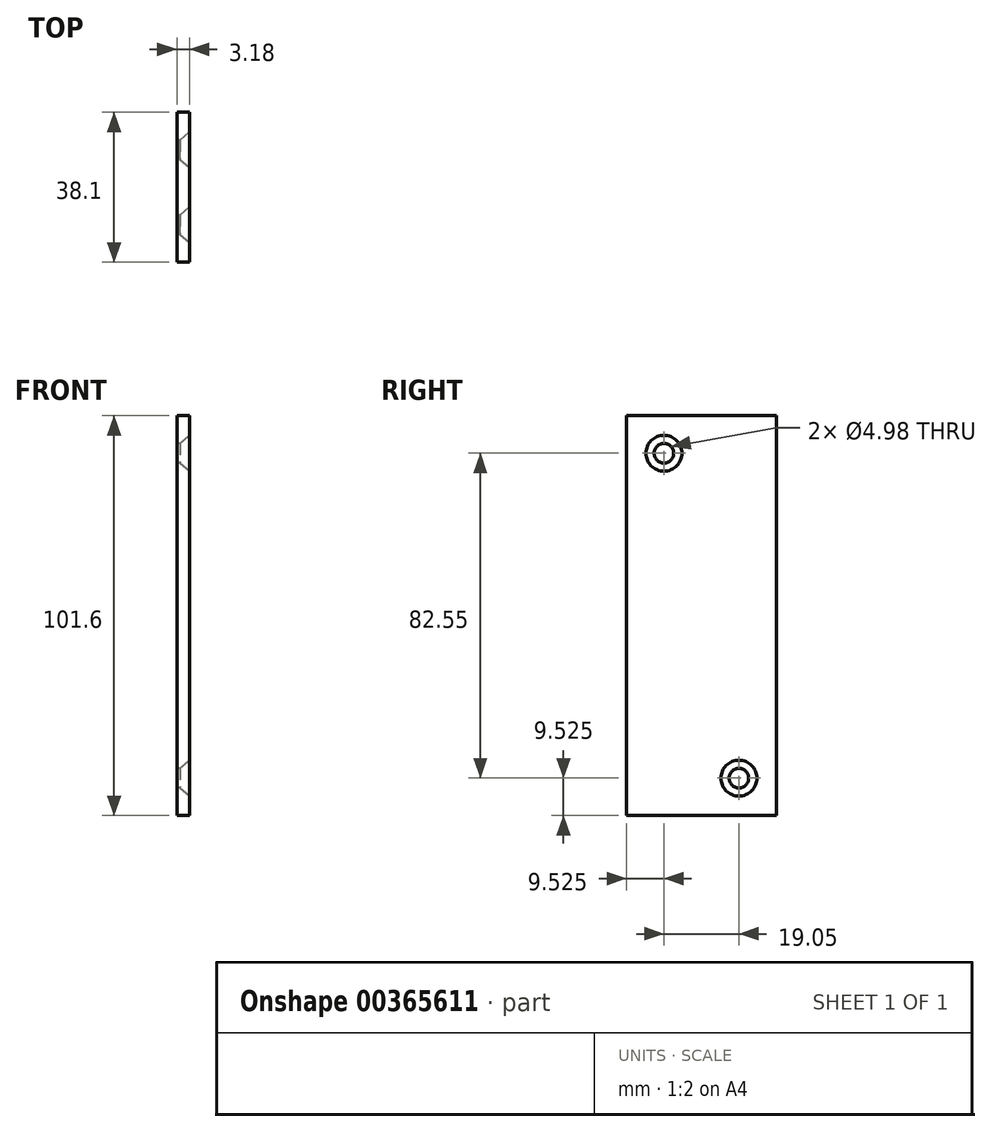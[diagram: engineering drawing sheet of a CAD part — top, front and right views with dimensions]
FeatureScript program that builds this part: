
annotation { "Feature Type Name" : "Feature", "Feature Type Description" : "" }
export const myFeature = defineFeature(function(context is Context, id is Id, definition is map)
    precondition{}
    {
        {
            var Q0;
            Q0=qCreatedBy(makeId("Right.planeOp"),FACE);
            var sketch = newSketch(context, id + "F0", { "sketchPlane" : qUnion([Q0])});
            skLineSegment(sketch, "E0.bottom", {"start": v(19.05, -50.8) * mm, "end": v(-19.05, -50.8) * mm});
            skLineSegment(sketch, "E0.top", {"start": v(19.05, 50.8) * mm, "end": v(-19.05, 50.8) * mm});
            skLineSegment(sketch, "E0.left", {"start": v(19.05, -50.8) * mm, "end": v(19.05, 50.8) * mm});
            skLineSegment(sketch, "E0.right", {"start": v(-19.05, -50.8) * mm, "end": v(-19.05, 50.8) * mm});
            skPoint(sketch, "E0.middle", {"position": v(0, 0) * mm});
            skSolve(sketch);
        }
        {
            var Q0;
            Q0=qSketchRegion(id+"F0",true);
            extrude(context, id + "F1", {"entities" : qUnion([Q0]), "depth" : 3.17 * mm, "offsetDistance" : 25.4 * mm});
        }
        {
            var Q0;
            Q0=makeQuery(id+"F1.opExtrude","CAP_FACE",FACE,{"disambiguationData":[OSD([sQuery(id+"F0.wireOp",EDGE,"E0.bottom"),sQuery(id+"F0.wireOp",EDGE,"E0.top"),sQuery(id+"F0.wireOp",EDGE,"E0.left"),sQuery(id+"F0.wireOp",EDGE,"E0.right")])],"isStart":false});
            var sketch = newSketch(context, id + "F2", { "sketchPlane" : qUnion([Q0])});
            skPoint(sketch, "E1", {"position": v(-9.53, 41.28) * mm});
            skPoint(sketch, "E2", {"position": v(9.53, -41.27) * mm});
            skSolve(sketch);
        }
        {
            var Q0;
            Q0=sQuery(id+"F2.wireOp",VERTEX,"E1");
            var Q1;
            Q1=sQuery(id+"F2.wireOp",VERTEX,"9c431e09-931f-43e2-840f-4f00e6efbce6");
            var Q2;
            Q2=sQuery(id+"F2.wireOp",VERTEX,"E2");
            var Q3;
            Q3=sQuery(id+"F2.wireOp",VERTEX,"9e30ab42-1027-4ecf-a6f1-ec90ac2d1b19");
            var Q4;
            Q4=makeQuery(id+"F1.opExtrude","SWEPT_BODY",BODY,{"disambiguationData":[OSD([sQuery(id+"F0.wireOp",EDGE,"E0.bottom"),sQuery(id+"F0.wireOp",EDGE,"E0.top"),sQuery(id+"F0.wireOp",EDGE,"E0.left"),sQuery(id+"F0.wireOp",EDGE,"E0.right")])]});
            hole(context, id + "F3", {"style" : HoleStyle.C_SINK, "endStyle" : HoleEndStyle.THROUGH, "standardTappedOrClearance" : lookupTablePath({ "fit" : "Normal (ASME)", "standard" : "ANSI", "size" : "#8", "type" : "Clearance" }), "standardBlindInLast" : lookupTablePath({ "fit" : "Normal", "standard" : "ANSI", "size" : "#8", "type" : "Clearance" }), "holeDiameter" : 4.98 * mm, "cSinkDiameter" : 9.12 * mm, "cSinkAngle" : 82 * degree, "majorDiameter" : 6.35 * mm, "isTappedThrough" : true, "tappedDepth" : 12.7 * mm, "tapClearance" : 3, "locations" : qUnion([Q0, Q1, Q2, Q3]), "scope" : qUnion([Q4]), "startStyle" : HoleStartStyle.SKETCH});
        }
    });
